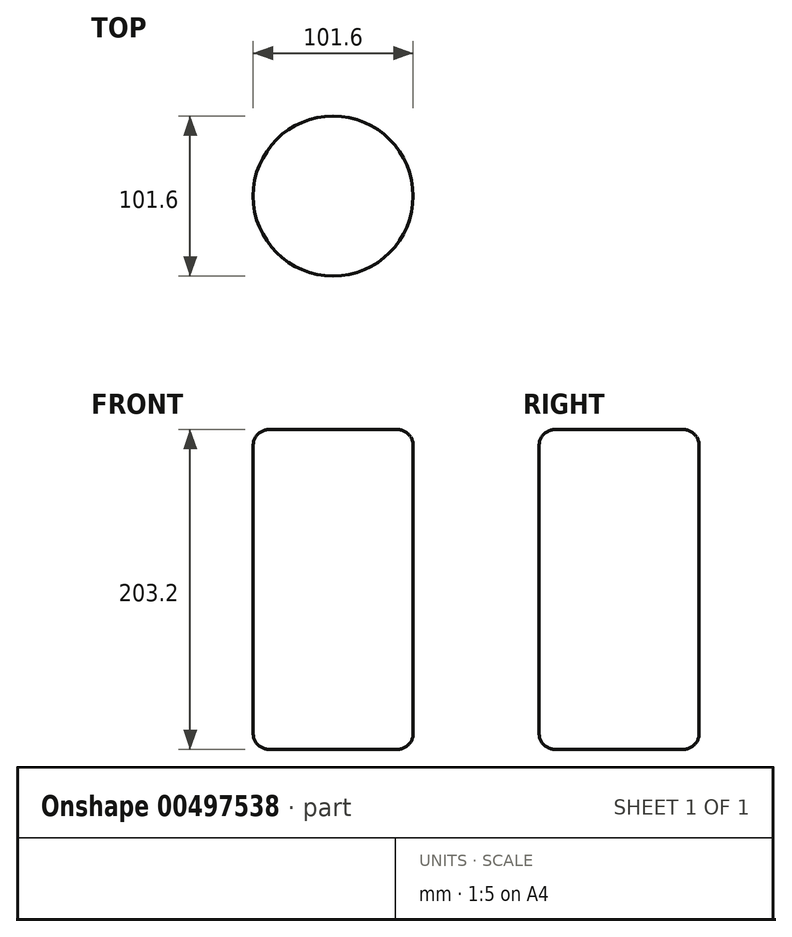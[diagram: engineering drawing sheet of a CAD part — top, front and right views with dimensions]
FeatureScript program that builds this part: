
annotation { "Feature Type Name" : "Feature", "Feature Type Description" : "" }
export const myFeature = defineFeature(function(context is Context, id is Id, definition is map)
    precondition{}
    {
        {
            var Q0;
            Q0=qCreatedBy(makeId("Top.planeOp"),FACE);
            var sketch = newSketch(context, id + "F0", { "sketchPlane" : qUnion([Q0])});
            skCircle(sketch, "E0", {"center": v(0, 0) * mm, "radius": 50.8 * mm});
            skSolve(sketch);
        }
        {
            var Q0;
            Q0 = qSketchRegion(id + "F0", true);
            extrude(context, id + "F1", {"entities" : qUnion([Q0]), "depth" : 203.2 * mm});
        }
        {
            var Q0;
            Q0=makeQuery(id+"F1.opExtrude","CAP_FACE",FACE,{"disambiguationData":[OSD([sQuery(id+"F0.wireOp",EDGE,"E0")])],"isStart":true});
            var Q1;
            Q1=makeQuery(id+"F1.opExtrude","CAP_FACE",FACE,{"disambiguationData":[OSD([sQuery(id+"F0.wireOp",EDGE,"E0")])],"isStart":false});
            fillet(context, id + "F2", {"entities" : qUnion([Q0, Q1]), "radius" : 10.16 * mm, "tangentPropagation" : true, "allowEdgeOverflow" : false});
        }
    });
